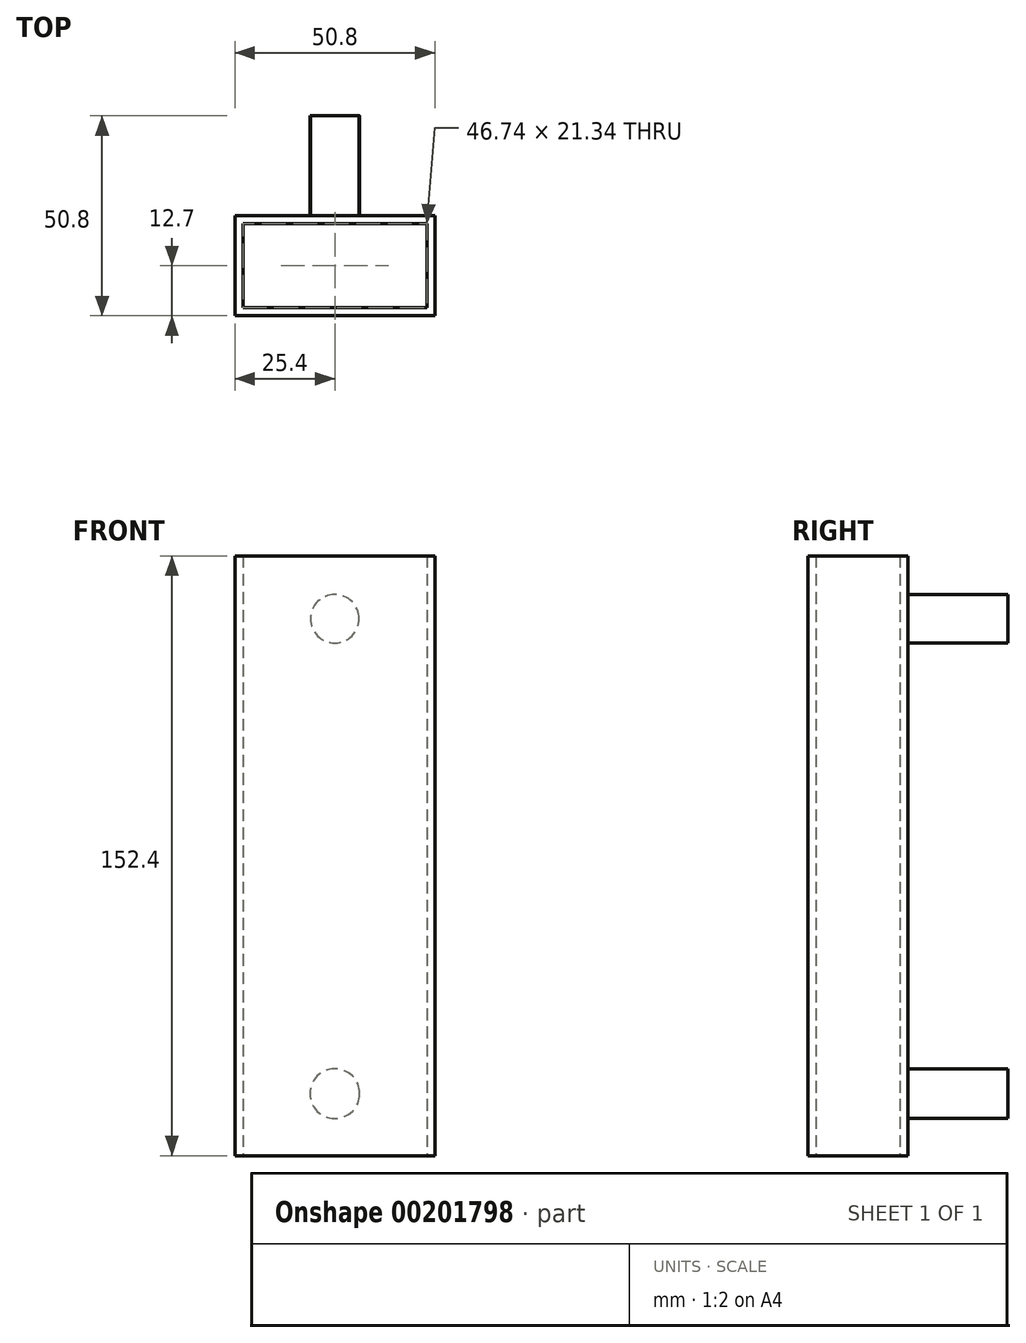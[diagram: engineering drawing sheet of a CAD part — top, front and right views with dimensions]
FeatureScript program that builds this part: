
annotation { "Feature Type Name" : "Feature", "Feature Type Description" : "" }
export const myFeature = defineFeature(function(context is Context, id is Id, definition is map)
    precondition{}
    {
        {
            var Q0;
            Q0=qCreatedBy(makeId("Front.planeOp"),FACE);
            var sketch = newSketch(context, id + "F0", { "sketchPlane" : qUnion([Q0])});
            skCircle(sketch, "E0", {"center": v(0, -60.44) * mm, "radius": 6.34 * mm});
            skCircle(sketch, "E1", {"center": v(0, 60.24) * mm, "radius": 6.16 * mm});
            skSolve(sketch);
        }
        {
            var Q0;
            Q0=makeQuery(id+"F0.imprint","IMPRINT",FACE,{"disambiguationData":[TD([[makeQuery(id+"F0.imprint","IMPRINT",EDGE,{"derivedFrom":sQuery(id+"F0.wireOp",EDGE,"4eKLBN6M-63jB-8HUi-JXtb-gBIzGswrornl")}),1.0]])]});
            var Q1;
            Q1=makeQuery(id+"F0.imprint","IMPRINT",FACE,{"disambiguationData":[TD([[makeQuery(id+"F0.imprint","IMPRINT",EDGE,{"derivedFrom":sQuery(id+"F0.wireOp",EDGE,"E0")}),1.0]])]});
            var Q2;
            Q2=makeQuery(id+"F0.imprint","IMPRINT",FACE,{"disambiguationData":[TD([[makeQuery(id+"F0.imprint","IMPRINT",EDGE,{"derivedFrom":sQuery(id+"F0.wireOp",EDGE,"E1")}),1.0]])]});
            extrude(context, id + "F1", {"entities" : qUnion([Q0, Q1, Q2]), "oppositeDirection" : true, "depth" : 25.4 * mm});
        }
        {
            var Q0;
            Q0=qCreatedBy(makeId("Front.planeOp"),FACE);
            var sketch = newSketch(context, id + "F2", { "sketchPlane" : qUnion([Q0])});
            skLineSegment(sketch, "E2.bottom", {"start": v(25.4, 76.2) * mm, "end": v(-25.4, 76.2) * mm});
            skLineSegment(sketch, "E2.top", {"start": v(25.4, -76.2) * mm, "end": v(-25.4, -76.2) * mm});
            skLineSegment(sketch, "E2.left", {"start": v(25.4, 76.2) * mm, "end": v(25.4, -76.2) * mm});
            skLineSegment(sketch, "E2.right", {"start": v(-25.4, 76.2) * mm, "end": v(-25.4, -76.2) * mm});
            skPoint(sketch, "E2.middle", {"position": v(0, 0) * mm});
            skSolve(sketch);
        }
        {
            var Q0;
            Q0=makeQuery(id+"F2.imprint","IMPRINT",FACE,{"disambiguationData":[TD([[makeQuery(id+"F2.imprint","IMPRINT",EDGE,{"derivedFrom":sQuery(id+"F2.wireOp",EDGE,"E2.bottom")}),1.0]])]});
            extrude(context, id + "F3", {"entities" : qUnion([Q0]), "depth" : 25.4 * mm});
        }
        {
            var Q0;
            Q0=makeQuery(id+"F3.opExtrude","SWEPT_FACE",FACE,{"disambiguationData":[OSD([sQuery(id+"F2.wireOp",EDGE,"E2.bottom")])]});
            var Q1;
            Q1=makeQuery(id+"F3.opExtrude","SWEPT_FACE",FACE,{"disambiguationData":[OSD([sQuery(id+"F2.wireOp",EDGE,"E2.top")])]});
            shell(context, id + "F4", {"entities" : qUnion([Q0, Q1]), "thickness" : 2.03 * mm});
        }
    });
